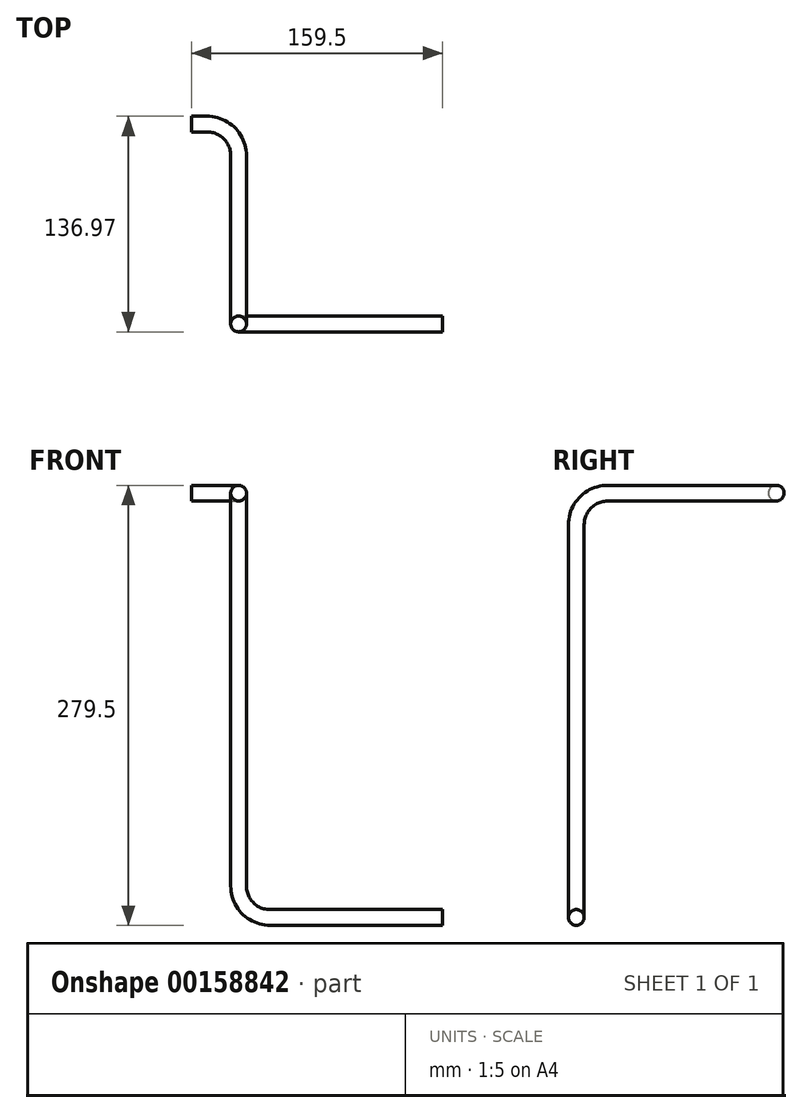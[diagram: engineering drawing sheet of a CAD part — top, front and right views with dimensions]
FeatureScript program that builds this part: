
annotation { "Feature Type Name" : "Feature", "Feature Type Description" : "" }
export const myFeature = defineFeature(function(context is Context, id is Id, definition is map)
    precondition{}
    {
        {
            var Q0;
            Q0=qCreatedBy(makeId("Top.planeOp"),FACE);
            var sketch = newSketch(context, id + "F0", { "sketchPlane" : qUnion([Q0])});
            skLineSegment(sketch, "E0", {"start": v(0, 0) * mm, "end": v(10, 0) * mm});
            skLineSegment(sketch, "E1", {"start": v(30, -20) * mm, "end": v(30, -106.97) * mm});
            skPoint(sketch, "E2.visualSharp", {"position": v(30, 0) * mm});
            skArc(sketch, "E2.filletArc", {"start": v(30, -20) * mm, "mid": v(24.14, -5.86) * mm, "end": v(10, 0) * mm});
            skSolve(sketch);
        }
        {
            var Q0;
            Q0=qCreatedBy(makeId("Right.planeOp"),FACE);
            var sketch = newSketch(context, id + "F1", { "sketchPlane" : qUnion([Q0])});
            skCircle(sketch, "E3", {"center": v(0, 0) * mm, "radius": 5 * mm});
            skSolve(sketch);
        }
        {
            var Q0;
            Q0=qCreatedBy(makeId("Front.planeOp"),FACE);
            cPlane(context, id + "F2", {"entities" : qUnion([Q0]), "cplaneType" : CPlaneType.OFFSET, "offset" : 126.97 * mm, "width" : 150 * mm, "height" : 150 * mm});
        }
        {
            var Q0;
            Q0=qCreatedBy(id+"F2.planeOp",FACE);
            var sketch = newSketch(context, id + "F3", { "sketchPlane" : qUnion([Q0])});
            skPoint(sketch, "E4.0", {"position": v(30, 0) * mm});
            skLineSegment(sketch, "E5", {"start": v(30, -20) * mm, "end": v(30, -249.5) * mm});
            skLineSegment(sketch, "E6", {"start": v(50, -269.5) * mm, "end": v(159.5, -269.5) * mm});
            skPoint(sketch, "E7.visualSharp", {"position": v(30, -269.5) * mm});
            skArc(sketch, "E7.filletArc", {"start": v(30, -249.5) * mm, "mid": v(35.86, -263.64) * mm, "end": v(50, -269.5) * mm});
            skSolve(sketch);
        }
        {
            var Q0;
            Q0=qCreatedBy(makeId("Right.planeOp"),FACE);
            cPlane(context, id + "F4", {"entities" : qUnion([Q0]), "cplaneType" : CPlaneType.OFFSET, "offset" : 30 * mm, "width" : 150 * mm, "height" : 150 * mm});
        }
        {
            var Q0;
            Q0=qCreatedBy(id+"F4.planeOp",FACE);
            var sketch = newSketch(context, id + "F5", { "sketchPlane" : qUnion([Q0])});
            skPoint(sketch, "E8.0", {"position": v(-126.97, -20) * mm});
            skLineSegment(sketch, "E9", {"start": v(-126.97, -20) * mm, "end": v(-126.97, -20) * mm});
            skLineSegment(sketch, "E10", {"start": v(-106.97, 0) * mm, "end": v(-106.97, 0) * mm});
            skPoint(sketch, "E11.visualSharp", {"position": v(-126.97, 0) * mm});
            skArc(sketch, "E11.filletArc", {"start": v(-106.97, 0) * mm, "mid": v(-121.12, -5.86) * mm, "end": v(-126.97, -20) * mm});
            skSolve(sketch);
        }
        {
            var Q0;
            Q0=makeQuery(id+"F1.imprint","IMPRINT",FACE,{"disambiguationData":[TD([[makeQuery(id+"F1.imprint","IMPRINT",EDGE,{"derivedFrom":sQuery(id+"F1.wireOp",EDGE,"E3")}),1.0]])]});
            var Q1;
            Q1=sQuery(id+"F0.wireOp",EDGE,"E0");
            var Q2;
            Q2=sQuery(id+"F0.wireOp",EDGE,"E2.filletArc");
            var Q3;
            Q3=sQuery(id+"F0.wireOp",EDGE,"E1");
            var Q4;
            Q4=sQuery(id+"F5.wireOp",EDGE,"E11.filletArc");
            var Q5;
            Q5=sQuery(id+"F3.wireOp",EDGE,"E5");
            var Q6;
            Q6=sQuery(id+"F3.wireOp",EDGE,"E7.filletArc");
            var Q7;
            Q7=sQuery(id+"F3.wireOp",EDGE,"E6");
            sweep(context, id + "F6", {"profiles" : qUnion([Q0]), "path" : qUnion([Q1, Q2, Q3, Q4, Q5, Q6, Q7])});
        }
    });
